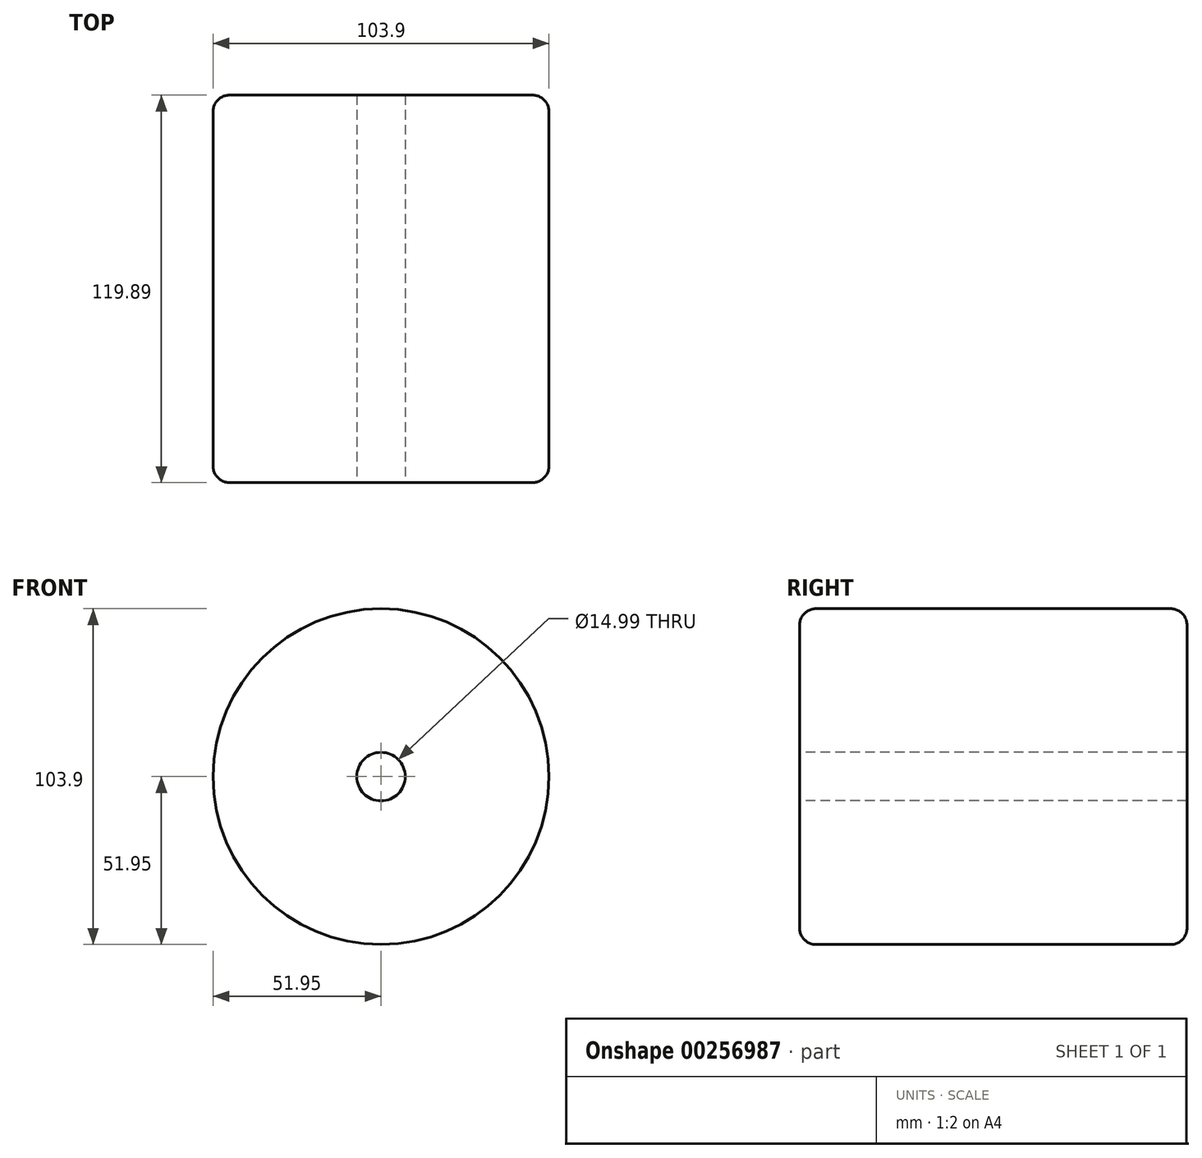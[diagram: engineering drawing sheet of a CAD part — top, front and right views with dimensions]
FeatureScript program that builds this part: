
annotation { "Feature Type Name" : "Feature", "Feature Type Description" : "" }
export const myFeature = defineFeature(function(context is Context, id is Id, definition is map)
    precondition{}
    {
        {
            var Q0;
            Q0=qCreatedBy(makeId("Front.planeOp"),FACE);
            var sketch = newSketch(context, id + "F0", { "sketchPlane" : qUnion([Q0])});
            skCircle(sketch, "E0", {"center": v(0, 0) * mm, "radius": 51.95 * mm});
            skSolve(sketch);
        }
        {
            var Q0;
            Q0=makeQuery(id+"F0.imprint","IMPRINT",FACE,{"disambiguationData":[TD([[makeQuery(id+"F0.imprint","IMPRINT",EDGE,{"derivedFrom":sQuery(id+"F0.wireOp",EDGE,"E0")}),1.0]])]});
            extrude(context, id + "F1", {"entities" : qUnion([Q0]), "depth" : 25.4 * mm});
        }
        {
            var Q0;
            Q0=makeQuery(id+"F1.opExtrude","CAP_FACE",FACE,{"disambiguationData":[OSD([sQuery(id+"F0.wireOp",EDGE,"E0")])],"isStart":false});
            extrude(context, id + "F2", {"entities" : qUnion([Q0]), "operationType" : NewBodyOperationType.ADD, "depth" : 94.49 * mm});
        }
        {
            var Q0;
            Q0=makeQuery(id+"F2.opExtrude","CAP_FACE",FACE,{"disambiguationData":[OSD([sQuery(id+"F0.wireOp",EDGE,"E0")])],"isStart":false});
            var sketch = newSketch(context, id + "F3", { "sketchPlane" : qUnion([Q0])});
            skSolve(sketch);
        }
        {
            var Q0;
            Q0=makeQuery(id+"F3.imprint","IMPRINT",FACE,{"disambiguationData":[TD([[makeQuery(id+"F3.imprint","IMPRINT",EDGE,{"derivedFrom":makeQuery(id+"F2.opExtrude","CAP_EDGE",EDGE,{"disambiguationData":[OSD([sQuery(id+"F0.wireOp",EDGE,"E0")])],"isStart":false})}),1.0]])]});
            var sketch = newSketch(context, id + "F4", { "sketchPlane" : qUnion([Q0])});
            skCircle(sketch, "E1", {"center": v(0, 0) * mm, "radius": 11.43 * mm});
            skSolve(sketch);
        }
        {
            var Q0;
            Q0=sQuery(id+"F4.wireOp",VERTEX,"E1.center");
            var Q1;
            Q1=makeQuery(id+"F1.opExtrude","SWEPT_BODY",BODY,{"disambiguationData":[OSD([sQuery(id+"F0.wireOp",EDGE,"E0")])]});
            hole(context, id + "F5", {"style" : HoleStyle.SIMPLE, "endStyle" : HoleEndStyle.THROUGH, "holeDiameter" : 15 * mm, "tappedDepth" : 12.7 * mm, "tapClearance" : 3, "startFromSketch" : true, "locations" : qUnion([Q0]), "scope" : qUnion([Q1])});
        }
        {
            var Q0;
            Q0=makeQuery(id+"F5.hole-0.boolean.opBoolean","COPY",EDGE,{"derivedFrom":makeQuery(id+"F5.hole-0.opRevolve","SWEPT_EDGE",EDGE,{"disambiguationData":[OSD([sQuery(id+"F5.hole-0.sketch.wireOp",EDGE,"core_line_2"),sQuery(id+"F5.hole-0.sketch.wireOp",EDGE,"core_line_3")])]})});
            var Q1;
            Q1=makeQuery(id+"F2.opExtrude","CAP_EDGE",EDGE,{"disambiguationData":[OSD([sQuery(id+"F0.wireOp",EDGE,"E0")])],"isStart":false});
            var Q2;
            Q2=makeQuery(id+"F1.opExtrude","CAP_EDGE",EDGE,{"disambiguationData":[OSD([sQuery(id+"F0.wireOp",EDGE,"E0")])],"isStart":true});
            var Q3;
            Q3=makeQuery(id+"F5.hole-0.boolean.opBoolean","INTERSECT",EDGE,{"derivedFrom":[makeQuery(id+"F1.opExtrude","CAP_FACE",FACE,{"disambiguationData":[OSD([sQuery(id+"F0.wireOp",EDGE,"E0")])],"isStart":true}),makeQuery(id+"F5.hole-0.opRevolve","SWEPT_FACE",FACE,{"disambiguationData":[OSD([sQuery(id+"F5.hole-0.sketch.wireOp",EDGE,"core_line_2")])]})]});
            fillet(context, id + "F6", {"entities" : qUnion([Q0, Q1, Q2, Q3]), "radius" : 5.08 * mm, "tangentPropagation" : true, "allowEdgeOverflow" : false});
        }
    });
